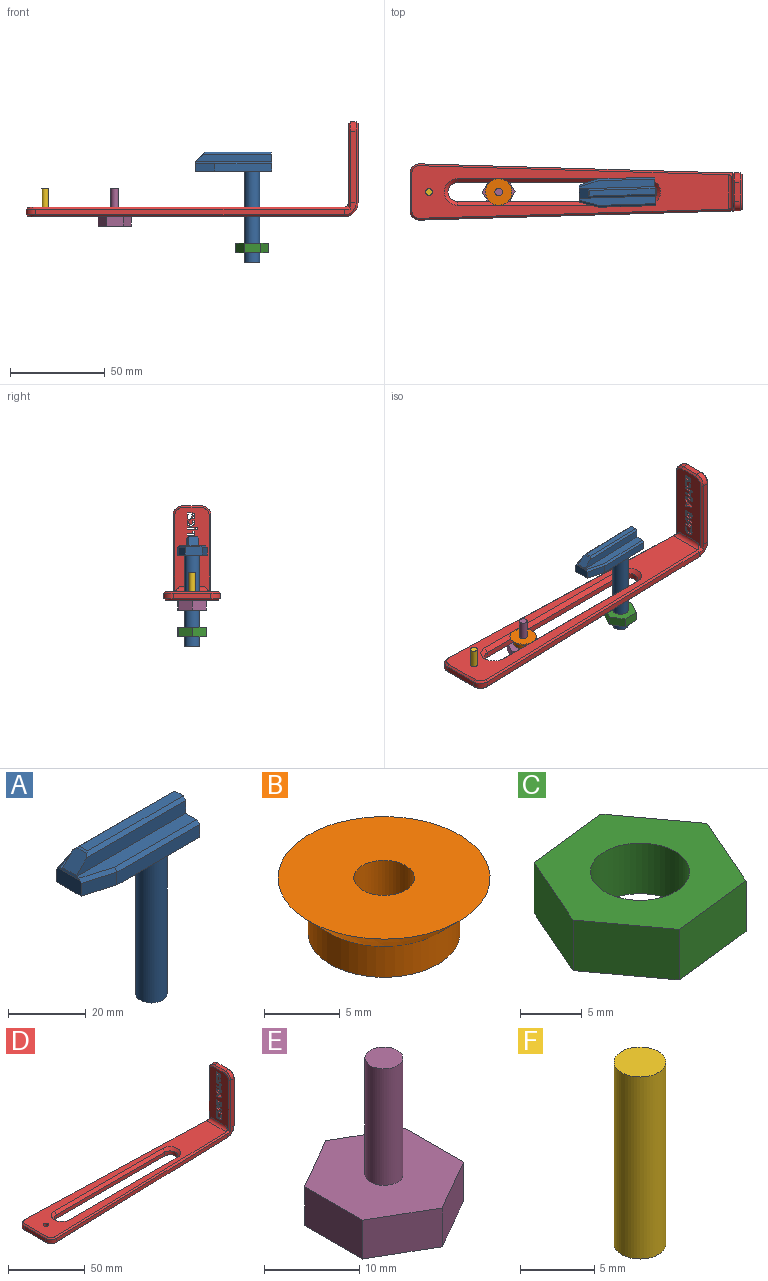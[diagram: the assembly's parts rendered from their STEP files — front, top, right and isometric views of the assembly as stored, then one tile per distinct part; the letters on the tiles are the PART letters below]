
ASSEMBLY  parts=6 mates=9
PART A: 23 faces, bbox 40x15x58 mm
  f0: plane 39.83x4mm, normal (0,0,1), area 144.4mm2, adj f4,f12,f18,f20,f22
  f1: plane 30x4mm, normal (0,1,0), area 120mm2, adj f4,f6,f9,f19
  f2: plane 9x4.59mm, normal (-1,0,0), area 40.9mm2, adj f6,f9,f10,f20,f21,f22
  f3: plane 30x4mm, normal (0,-1,0), area 120mm2, adj f4,f6,f10,f18
  f4: plane 15x10mm, normal (1,0,0), area 98mm2, adj f0,f1,f3,f5,f6,f11,f12,f13
  f5: plane 39.83x4mm, normal (0,0,1), area 144.4mm2, adj f4,f11,f19,f21,f22
  f6: plane 40x15mm, normal (0,0,-1), area 519.7mm2, adj f1,f2,f3,f4,f7,f9,f10
  f7: cylinder r=4mm len=48mm, axis (0,0,1), area 1206.4mm2, adj f6,f8
  f8: plane 8x8mm, normal (0,0,-1), area 50.3mm2, adj f7
  f9: plane 10x4mm, normal (-0.29,0.96,0), area 41.8mm2, adj f1,f2,f6,f21
  f10: plane 10x4mm, normal (-0.29,-0.96,0), area 41.8mm2, adj f2,f3,f6,f20
  f11: plane 39.83x4mm, normal (0,1,0), area 152mm2, adj f4,f5,f14,f15,f22
  f12: plane 39.83x4mm, normal (0,-1,0), area 152mm2, adj f0,f4,f14,f16,f22
  f13: plane 34.59x3mm, normal (0,0,1), area 103.8mm2, adj f4,f15,f16,f17
  f14: plane 5x4.41mm, normal (-0.71,0,0.71), area 30.5mm2, adj f11,f12,f15,f16,f17,f22
  f15: plane 36x1mm, normal (0,0.71,0.71), area 50.1mm2, adj f4,f11,f13,f14,f17
  f16: plane 36x1mm, normal (0,-0.71,0.71), area 50.1mm2, adj f4,f12,f13,f14,f17
  f17: plane 3.59x0.71mm, normal (-0.38,0,0.92), area 2.5mm2, adj f13,f14,f15,f16
  f18: plane 30x1mm, normal (0,-0.71,0.71), area 42.3mm2, adj f0,f3,f4,f20
  f19: plane 30x1mm, normal (0,0.71,0.71), area 42.3mm2, adj f1,f4,f5,f21
  f20: plane 10.15x3.99mm, normal (-0.2,-0.68,0.71), area 14.8mm2, adj f0,f2,f10,f18,f22
  f21: plane 10.15x3.99mm, normal (-0.2,0.68,0.71), area 14.8mm2, adj f2,f5,f9,f19,f22
  f22: plane 7.78x0.71mm, normal (-0.92,0,0.38), area 4.9mm2, adj f0,f2,f5,f11,f12,f14,f20,f21
PART B: 5 faces, bbox 14x14x4.5 mm
  f0: cylinder r=2mm len=4.5mm, axis (0,0,-1), area 56.5mm2, adj f2,f4
  f1: cylinder r=5mm len=10mm, axis (0,0,-1), area 78.5mm2, adj f2,f3
  f2: plane 10x10mm, normal (0,0,-1), area 66mm2, adj f0,f1
  f3: cone r=7mm half-angle=45deg, axis (0,0,1), area 106.6mm2, adj f1,f4
  f4: plane 14x14mm, normal (0,0,1), area 141.4mm2, adj f0,f3
PART C: 9 faces, bbox 17.2x15.9x5 mm
  f0: plane 6.98x5.13mm, normal (0.81,0.59,0), area 43.3mm2, adj f1,f5,f6,f7
  f1: plane 8.61x5mm, normal (-0.11,0.99,0), area 43.3mm2, adj f0,f2,f6,f7
  f2: plane 7.93x5mm, normal (-0.92,0.4,0), area 43.3mm2, adj f1,f3,f6,f7
  f3: plane 6.98x5.13mm, normal (-0.81,-0.59,0), area 43.3mm2, adj f2,f4,f6,f7
  f4: plane 8.61x5mm, normal (0.11,-0.99,0), area 43.3mm2, adj f3,f5,f6,f7
  f5: plane 7.93x5mm, normal (0.92,-0.4,0), area 43.3mm2, adj f0,f4,f6,f7
  f6: plane 17.21x15.87mm, normal (0,0,1), area 144.6mm2, adj f0,f1,f2,f3,f4,f5,f8
  f7: plane 17.21x15.87mm, normal (0,0,-1), area 144.6mm2, adj f0,f1,f2,f3,f4,f5,f8
  f8: cylinder r=4mm len=8mm, axis (0,0,1), area 125.7mm2, adj f6,f7
PART D: 179 faces, bbox 175.8x30.5x50.8 mm
  f0: plane 41.7x18mm, normal (1,0,0), area 663.1mm2, adj f17,f27,f28,f29,f30,f31,f32,f33
  f1: plane 44x18mm, normal (-1,0,0), area 668.4mm2, adj f18,f27,f28,f29,f30,f31,f32,f33
  f2: plane 162.55x4.78mm, normal (0.03,-1,0), area 487.9mm2, adj f3,f15,f160,f172
  f3: cylinder r=5mm len=5.15mm, axis (0,0,1), area 24mm2, adj f2,f4,f159,f173
  f4: plane 19.7x3mm, normal (-1,0,0), area 59.1mm2, adj f3,f5,f158,f174
  f5: cylinder r=5mm len=5.15mm, axis (0,0,1), area 24mm2, adj f4,f7,f157,f175
  f6: cylinder r=1.75mm len=5mm, axis (0,0,1), area 55mm2, adj f8,f9
  f7: plane 162.55x4.78mm, normal (0.03,1,0), area 487.9mm2, adj f5,f16,f156,f176
  f8: plane 166.7x27.7mm, normal (0,0,-1), area 2744.8mm2, adj f6,f17,f19,f20,f21,f22,f172,f173
  f9: plane 166.7x27.7mm, normal (0,0,1), area 2269.4mm2, adj f6,f18,f23,f24,f25,f26,f155,f156
  f10: plane 10x3mm, normal (0,0,1), area 30mm2, adj f13,f14,f164,f169
  f11: plane 37.72x3.01mm, normal (0,-1,0), area 113.1mm2, adj f13,f15,f162,f167
  f12: plane 37.72x3.01mm, normal (0,1,0), area 113.1mm2, adj f14,f16,f166,f171
  f13: cylinder r=5mm len=5mm, axis (1,0,0), area 23.6mm2, adj f10,f11,f163,f168
  f14: cylinder r=5mm len=5mm, axis (1,0,0), area 23.6mm2, adj f10,f12,f165,f170
  f15: bspline ~11.61x7.3mm, area 19.2mm2, adj f2,f11,f161,f162,f178
  f16: bspline ~11.61x7.3mm, area 19.2mm2, adj f7,f12,f155,f166,f177
  f17: cylinder r=7.3mm len=18.14mm, axis (0,-1,0), area 207.2mm2, adj f0,f8,f177,f178
  f18: cylinder r=2.3mm len=18.13mm, axis (0,-1,0), area 56.9mm2, adj f1,f9,f155,f161
  f19: cylinder r=5mm len=10mm, axis (0,0,-1), area 47.1mm2, adj f8,f20,f22,f25
  f20: plane 100x3mm, normal (0,-1,0), area 300mm2, adj f8,f19,f21,f26
  f21: cylinder r=5mm len=10mm, axis (0,0,-1), area 47.1mm2, adj f8,f20,f22,f24
  f22: plane 100x3mm, normal (0,1,0), area 300mm2, adj f8,f19,f21,f23
  f23: plane 100x2mm, normal (0,0.71,0.71), area 282.8mm2, adj f9,f22,f24,f25
  f24: cone r=7mm half-angle=45deg, axis (0,0,1), area 53.3mm2, adj f9,f21,f23,f26
  f25: cone r=7mm half-angle=45deg, axis (0,0,1), area 53.3mm2, adj f9,f19,f23,f26
  f26: plane 100x2mm, normal (0,-0.71,0.71), area 282.8mm2, adj f9,f20,f24,f25
  f27: plane 5x0.03mm, normal (0,-1,0), area 0.1mm2, adj f0,f1,f28,f29
  f28: extruded ~5x0.54mm, area 3.6mm2, adj f0,f1,f27,f30
  f29: plane 5x0.52mm, normal (0,-0.36,0.93), area 2.8mm2, adj f0,f1,f27,f44
  f30: extruded ~5x0.72mm, area 3.7mm2, adj f0,f1,f28,f31
  f31: extruded ~5x0.86mm, area 4.7mm2, adj f0,f1,f30,f32
  f32: extruded ~5x0.89mm, area 4.8mm2, adj f0,f1,f31,f33
  f33: extruded ~5x0.89mm, area 5.1mm2, adj f0,f1,f32,f34
  f34: extruded ~5x1.27mm, area 6.6mm2, adj f0,f1,f33,f35
  f35: plane 5x0.66mm, normal (0,1,0.03), area 3.3mm2, adj f0,f1,f34,f36
  f36: plane 5x0.17mm, normal (0,0,1), area 0.8mm2, adj f0,f1,f35,f37
  f37: extruded ~5x0.59mm, area 4.7mm2, adj f0,f1,f36,f38
  f38: extruded ~5x1.07mm, area 5.6mm2, adj f0,f1,f37,f39
  f39: plane 5x0.7mm, normal (0,-0.44,0.9), area 3.9mm2, adj f0,f1,f38,f40
  f40: extruded ~5x1.45mm, area 7.5mm2, adj f0,f1,f39,f41
  f41: extruded ~5x1.17mm, area 6.2mm2, adj f0,f1,f40,f42
  f42: extruded ~5x1.01mm, area 5.6mm2, adj f0,f1,f41,f43
  f43: plane 5x2.53mm, normal (0,0,-1), area 12.6mm2, adj f0,f1,f42,f44
  f44: plane 5x0.72mm, normal (0,-1,0), area 3.6mm2, adj f0,f1,f29,f43
  f45: plane 5x4.96mm, normal (0,0,-1), area 24.8mm2, adj f0,f1,f46,f56
  f46: plane 5x0.95mm, normal (0,1,0), area 4.7mm2, adj f0,f1,f45,f47
  f47: plane 5x2.35mm, normal (0,0,1), area 11.7mm2, adj f0,f1,f46,f48
  f48: extruded ~5x1.37mm, area 6.8mm2, adj f0,f1,f47,f49
  f49: plane 5x0.02mm, normal (0,1,0), area 0.1mm2, adj f0,f1,f48,f50
  f50: plane 5x3.71mm, normal (0,0.5,-0.87), area 21.5mm2, adj f0,f1,f49,f51
  f51: plane 5x1.33mm, normal (0,1,0), area 6.6mm2, adj f0,f1,f50,f52
  f52: plane 5x4.96mm, normal (0,0,1), area 24.8mm2, adj f0,f1,f51,f53
  f53: plane 5x0.94mm, normal (0,-1,0), area 4.7mm2, adj f0,f1,f52,f54
  f54: plane 5x2.33mm, normal (0,0,-1), area 11.7mm2, adj f0,f1,f53,f55
  f55: extruded ~5x1.42mm, area 7.1mm2, adj f0,f1,f54,f57
  f56: plane 5x1.34mm, normal (0,-1,0), area 6.7mm2, adj f0,f1,f45,f58
  f57: plane 5x0.03mm, normal (0,-1,0), area 0.2mm2, adj f0,f1,f55,f58
  f58: plane 5x3.75mm, normal (0,-0.5,0.87), area 21.6mm2, adj f0,f1,f56,f57
  f59: plane 5x0.88mm, normal (0,0,1), area 4.4mm2, adj f0,f1,f60,f75
  f60: plane 5x0.94mm, normal (0,-1,0), area 4.7mm2, adj f0,f1,f59,f61
  f61: plane 5x1.03mm, normal (0,0,1), area 5.2mm2, adj f0,f1,f60,f62
  f62: extruded ~5x0.67mm, area 3.4mm2, adj f0,f1,f61,f63
  f63: extruded ~5x0.96mm, area 5.5mm2, adj f0,f1,f62,f64
  f64: extruded ~5x1.23mm, area 6.5mm2, adj f0,f1,f63,f65
  f65: extruded ~5x1.23mm, area 6.6mm2, adj f0,f1,f64,f66
  f66: extruded ~5x1.09mm, area 6.1mm2, adj f0,f1,f65,f67
  f67: extruded ~5x1.13mm, area 5.9mm2, adj f0,f1,f66,f68
  f68: plane 5x0.84mm, normal (0,-0.38,-0.92), area 4.6mm2, adj f0,f1,f67,f69
  f69: extruded ~5x1.47mm, area 7.6mm2, adj f0,f1,f68,f70
  f70: extruded ~5x1.9mm, area 10.4mm2, adj f0,f1,f69,f71
  f71: extruded ~5x1.87mm, area 10.2mm2, adj f0,f1,f70,f72
  f72: extruded ~5x1.89mm, area 10.2mm2, adj f0,f1,f71,f73
  f73: extruded ~5x1.71mm, area 9.5mm2, adj f0,f1,f72,f74
  f74: extruded ~5x0.86mm, area 4.3mm2, adj f0,f1,f73,f76
  f75: plane 5x1.97mm, normal (0,1,0), area 9.8mm2, adj f0,f1,f59,f77
  f76: extruded ~5x0.9mm, area 4.6mm2, adj f0,f1,f74,f77
  f77: plane 5x2.57mm, normal (0,0,-1), area 12.9mm2, adj f0,f1,f75,f76
  f78: plane 5x0.78mm, normal (0,0,-1), area 3.9mm2, adj f0,f1,f79,f93
  f79: plane 5x0.9mm, normal (0,1,0), area 4.5mm2, adj f0,f1,f78,f80
  f80: plane 5x0.24mm, normal (0,0,-1), area 1.2mm2, adj f0,f1,f79,f81
  f81: extruded ~5x0.33mm, area 1.8mm2, adj f0,f1,f80,f82
  f82: extruded ~5x0.32mm, area 1.8mm2, adj f0,f1,f81,f83
  f83: extruded ~5x0.58mm, area 2.9mm2, adj f0,f1,f82,f84
  f84: plane 5x0.76mm, normal (0,-0.33,-0.94), area 4mm2, adj f0,f1,f83,f85
  f85: extruded ~5x0.95mm, area 4.9mm2, adj f0,f1,f84,f86
  f86: extruded ~5x1.02mm, area 5.4mm2, adj f0,f1,f85,f87
  f87: extruded ~5x0.95mm, area 5.1mm2, adj f0,f1,f86,f88
  f88: plane 5x0.28mm, normal (0,0,1), area 1.4mm2, adj f0,f1,f87,f89
  f89: plane 5x0.57mm, normal (0,0.9,0.44), area 3.2mm2, adj f0,f1,f88,f90
  f90: plane 5x0.5mm, normal (0,0,1), area 2.5mm2, adj f0,f1,f89,f91
  f91: plane 5x0.57mm, normal (0,-1,0), area 2.8mm2, adj f0,f1,f90,f92
  f92: plane 5x3.01mm, normal (0,0,1), area 15.1mm2, adj f0,f1,f91,f94
  f93: plane 5x0.9mm, normal (0,-1,0), area 4.5mm2, adj f0,f1,f78,f95
  f94: plane 5x1.03mm, normal (0,-1,0), area 5.2mm2, adj f0,f1,f92,f95
  f95: plane 5x3.01mm, normal (0,0,-1), area 15.1mm2, adj f0,f1,f93,f94
  f96: extruded ~5x0.65mm, area 3.5mm2, adj f0,f1,f97,f106
  f97: extruded ~5x0.51mm, area 3.5mm2, adj f0,f1,f96,f98
  f98: plane 5x0.05mm, normal (0,1,0), area 0.2mm2, adj f0,f1,f97,f99
  f99: plane 5x0.64mm, normal (0,0.23,-0.97), area 3.3mm2, adj f0,f1,f98,f100
  f100: plane 5x0.78mm, normal (0,1,0), area 3.9mm2, adj f0,f1,f99,f101
  f101: plane 5x3.79mm, normal (0,0,1), area 19mm2, adj f0,f1,f100,f102
  f102: plane 5x1.03mm, normal (0,-1,0), area 5.2mm2, adj f0,f1,f101,f103
  f103: plane 5x1.93mm, normal (0,0,-1), area 9.6mm2, adj f0,f1,f102,f104
  f104: extruded ~5x0.71mm, area 3.9mm2, adj f0,f1,f103,f105
  f105: extruded ~5x0.77mm, area 4.2mm2, adj f0,f1,f104,f107
  f106: extruded ~5x0.35mm, area 1.8mm2, adj f0,f1,f96,f108
  f107: extruded ~5x0.31mm, area 1.5mm2, adj f0,f1,f105,f108
  f108: plane 5x0.97mm, normal (0,-0.08,-1), area 4.9mm2, adj f0,f1,f106,f107
  f109: plane 5x1.81mm, normal (0,-1,0), area 9mm2, adj f0,f1,f110,f111
  f110: plane 5x1.18mm, normal (0,-0.29,-0.96), area 6.2mm2, adj f0,f1,f109,f112
  f111: plane 5x1.18mm, normal (0,-0.29,0.96), area 6.2mm2, adj f0,f1,f109,f116
  f112: plane 5x1.13mm, normal (0,-1,0), area 5.7mm2, adj f0,f1,f110,f113
  f113: plane 5x4.98mm, normal (0,0.33,0.94), area 26.4mm2, adj f0,f1,f112,f114
  f114: plane 5x1.28mm, normal (0,1,0), area 6.4mm2, adj f0,f1,f113,f115
  f115: plane 5x4.98mm, normal (0,0.33,-0.94), area 26.4mm2, adj f0,f1,f114,f116
  f116: plane 5x1.13mm, normal (0,-1,0), area 5.7mm2, adj f0,f1,f111,f115
  f117: extruded ~5x0.65mm, area 3.2mm2, adj f0,f1,f118,f128
  f118: extruded ~5x0.51mm, area 2.8mm2, adj f0,f1,f117,f119
  f119: plane 5x0.89mm, normal (0,0,-1), area 4.4mm2, adj f0,f1,f118,f120
  f120: extruded ~5x0.51mm, area 2.8mm2, adj f0,f1,f119,f121
  f121: extruded ~5x0.55mm, area 2.8mm2, adj f0,f1,f120,f122
  f122: extruded ~5x1.11mm, area 7.8mm2, adj f0,f1,f121,f123
  f123: extruded ~5x1.15mm, area 8mm2, adj f0,f1,f122,f124
  f124: extruded ~5x0.42mm, area 2.1mm2, adj f0,f1,f123,f125
  f125: extruded ~5x0.45mm, area 2.4mm2, adj f0,f1,f124,f126
  f126: plane 5x0.8mm, normal (0,-0.36,-0.93), area 4.3mm2, adj f0,f1,f125,f127
  f127: extruded ~5x1.18mm, area 6.1mm2, adj f0,f1,f126,f129
  f128: extruded ~5x1.94mm, area 15.1mm2, adj f0,f1,f117,f130
  f129: extruded ~5x1.38mm, area 7.6mm2, adj f0,f1,f127,f130
  f130: extruded ~5x1.48mm, area 8mm2, adj f0,f1,f128,f129
  f131: plane 5x3.79mm, normal (0,0,-1), area 19mm2, adj f0,f1,f132,f133
  f132: plane 5x1.03mm, normal (0,-1,0), area 5.2mm2, adj f0,f1,f131,f134
  f133: plane 5x1.03mm, normal (0,1,0), area 5.2mm2, adj f0,f1,f131,f134
  f134: plane 5x3.79mm, normal (0,0,1), area 19mm2, adj f0,f1,f132,f133
  f135: extruded ~5x0.56mm, area 4.4mm2, adj f0,f1,f136,f137
  f136: extruded ~5x0.42mm, area 2.3mm2, adj f0,f1,f135,f138
  f137: extruded ~5x0.56mm, area 4.3mm2, adj f0,f1,f135,f139
  f138: extruded ~5x0.38mm, area 2.1mm2, adj f0,f1,f136,f139
  f139: extruded ~5x0.56mm, area 4.3mm2, adj f0,f1,f137,f138
  f140: extruded ~5x0.55mm, area 2.8mm2, adj f0,f1,f141,f152
  f141: extruded ~5x0.56mm, area 3mm2, adj f0,f1,f140,f142
  f142: plane 5x0.86mm, normal (0,-0.37,-0.93), area 4.6mm2, adj f0,f1,f141,f143
  f143: extruded ~5x1.45mm, area 7.5mm2, adj f0,f1,f142,f144
  f144: extruded ~5x1.24mm, area 6.4mm2, adj f0,f1,f143,f145
  f145: extruded ~5x0.89mm, area 6.1mm2, adj f0,f1,f144,f146
  f146: extruded ~5x1.36mm, area 7mm2, adj f0,f1,f145,f147
  f147: extruded ~5x1.88mm, area 10.1mm2, adj f0,f1,f146,f148
  f148: extruded ~5x1.65mm, area 9.2mm2, adj f0,f1,f147,f149
  f149: extruded ~5x1.36mm, area 7mm2, adj f0,f1,f148,f150
  f150: plane 5x0.88mm, normal (0,0,-1), area 4.4mm2, adj f0,f1,f149,f151
  f151: extruded ~5x1.26mm, area 6.5mm2, adj f0,f1,f150,f153
  f152: extruded ~5x0.92mm, area 5.3mm2, adj f0,f1,f140,f154
  f153: extruded ~5x1.66mm, area 11.8mm2, adj f0,f1,f151,f154
  f154: extruded ~5x1.24mm, area 6.5mm2, adj f0,f1,f152,f153
  f155: bspline ~6.98x3.43mm, area 5.6mm2, adj f1,f9,f16,f18,f156,f166
  f156: plane 162.58x5.78mm, normal (0.02,0.71,0.71), area 230mm2, adj f7,f9,f155,f157
  f157: cone r=4mm half-angle=45deg, axis (0,0,-1), area 10.2mm2, adj f5,f9,f156,f158
  f158: plane 19.7x1mm, normal (-0.71,0,0.71), area 27.9mm2, adj f4,f9,f157,f159
  f159: cone r=4mm half-angle=45deg, axis (0,0,-1), area 10.2mm2, adj f3,f9,f158,f160
  f160: plane 162.58x5.78mm, normal (0.02,-0.71,0.71), area 230mm2, adj f2,f9,f159,f161
  f161: bspline ~6.98x3.43mm, area 5.6mm2, adj f1,f9,f15,f18,f160,f162
  f162: plane 41.8x1.81mm, normal (-0.71,-0.71,0), area 57.2mm2, adj f1,f11,f15,f161,f163
  f163: cone r=4mm half-angle=45deg, axis (1,0,0), area 10mm2, adj f1,f13,f162,f164
  f164: plane 10x1mm, normal (-0.71,0,0.71), area 14.1mm2, adj f1,f10,f163,f165
  f165: cone r=4mm half-angle=45deg, axis (1,0,0), area 10mm2, adj f1,f14,f164,f166
  f166: plane 41.8x1.81mm, normal (-0.71,0.71,0), area 57.2mm2, adj f1,f12,f16,f155,f165
  f167: plane 37.71x1mm, normal (0.71,-0.71,0), area 53.3mm2, adj f0,f11,f168,f178
  f168: cone r=4mm half-angle=45deg, axis (-1,0,0), area 10mm2, adj f0,f13,f167,f169
  f169: plane 10x1mm, normal (0.71,0,0.71), area 14.1mm2, adj f0,f10,f168,f170
  f170: cone r=4mm half-angle=45deg, axis (-1,0,0), area 10mm2, adj f0,f14,f169,f171
  f171: plane 37.71x1mm, normal (0.71,0.71,0), area 53.3mm2, adj f0,f12,f170,f177
  f172: plane 162.58x5.78mm, normal (0.02,-0.71,-0.71), area 230mm2, adj f2,f8,f173,f178
  f173: cone r=5mm half-angle=45deg, axis (0,0,1), area 10.2mm2, adj f3,f8,f172,f174
  f174: plane 19.7x1mm, normal (-0.71,0,-0.71), area 27.9mm2, adj f4,f8,f173,f175
  f175: cone r=5mm half-angle=45deg, axis (0,0,1), area 10.2mm2, adj f5,f8,f174,f176
  f176: plane 162.58x5.78mm, normal (0.02,0.71,-0.71), area 230mm2, adj f7,f8,f175,f177
  f177: bspline ~7.33x7.31mm, area 15.1mm2, adj f16,f17,f171,f176
  f178: bspline ~7.33x7.31mm, area 15.1mm2, adj f15,f17,f167,f172
PART E: 10 faces, bbox 15x17.3x20 mm
  f0: plane 7.5x5mm, normal (0.5,0.87,0), area 43.3mm2, adj f1,f5,f6,f7
  f1: plane 7.5x5mm, normal (-0.5,0.87,0), area 43.3mm2, adj f0,f2,f6,f7
  f2: plane 8.66x5mm, normal (-1,0,0), area 43.3mm2, adj f1,f3,f6,f7
  f3: plane 7.5x5mm, normal (-0.5,-0.87,0), area 43.3mm2, adj f2,f4,f6,f7
  f4: plane 7.5x5mm, normal (0.5,-0.87,0), area 43.3mm2, adj f3,f5,f6,f7
  f5: plane 8.66x5mm, normal (1,0,0), area 43.3mm2, adj f0,f4,f6,f7
  f6: plane 17.32x15mm, normal (0,0,1), area 182.3mm2, adj f0,f1,f2,f3,f4,f5,f8
  f7: plane 17.32x15mm, normal (0,0,-1), area 194.9mm2, adj f0,f1,f2,f3,f4,f5
  f8: cylinder r=2mm len=15mm, axis (0,0,-1), area 188.5mm2, adj f6,f9
  f9: plane 4x4mm, normal (0,0,1), area 12.6mm2, adj f8
PART F: 3 faces, bbox 3.5x3.5x15 mm
  f0: cylinder r=1.75mm len=15mm, axis (0,0,-1), area 164.9mm2, adj f1,f2
  f1: plane 3.5x3.5mm, normal (0,0,1), area 9.6mm2, adj f0
  f2: plane 3.5x3.5mm, normal (0,0,-1), area 9.6mm2, adj f0
PLACE A rot(axis=(0,0,1),1.7deg) t=(13.59,10.05,18.35)mm
PLACE B rot(axis=(0,0,-1),148.3deg) t=(-48.9,10.34,-5.15)mm
PLACE C rot(axis=(0,0,-1),4.7deg) t=(23.59,10.34,-24.78)mm
PLACE D t=(-10.63,10.34,-5.65)mm fixed
PLACE E rot(axis=(0,0,-1),148.3deg) t=(-48.9,10.34,-10.65)mm
PLACE F t=(-85.63,10.34,-5.65)mm
MATE parallel A.f3 <-> D.f2  axis (0.03,-1,0) through (18.81,2.7,20.35)mm
MATE slider E.f8 <-> B.f0  axis (0,0,-1) through (-48.9,10.34,1.85)mm
MATE fastened F.f0 <-> D.f6  axis (0,0,-1) through (-85.63,10.34,-5.65)mm
MATE pin_slot B.f1 <-> D.f21  axis (0,0,1) through (-48.9,10.34,-2.65)mm
MATE parallel C.f4 <-> D.f2  axis (0.03,-1,0) through (23.81,2.85,-22.28)mm
MATE parallel E.f0 <-> D.f2  axis (0.03,-1,0) through (-48.68,2.85,-8.15)mm
MATE pin_slot A.f7 <-> D.f21  axis (0,0,1) through (23.59,10.34,-5.65)mm
MATE cylindrical C.f8 <-> A.f7  axis (0,0,1) through (23.59,10.34,-24.78)mm
MATE parallel E.f8 <-> D.f8  axis (0,0,1) through (-48.9,10.34,-5.65)mm
